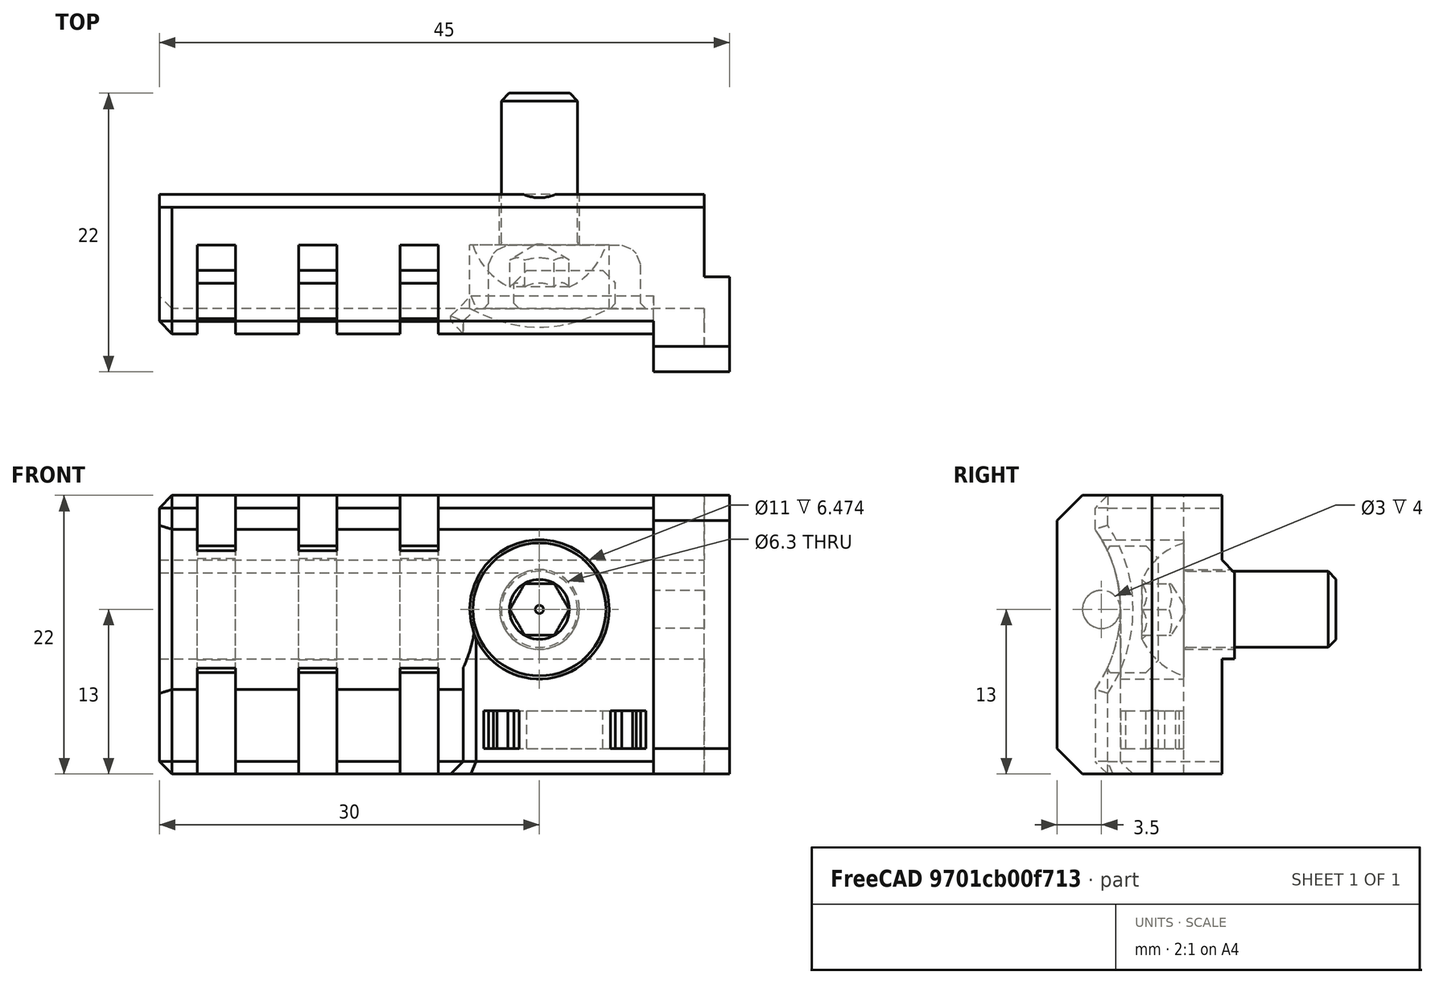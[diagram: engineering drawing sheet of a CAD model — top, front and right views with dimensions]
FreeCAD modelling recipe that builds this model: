
FCSTD DOCUMENT  (FreeCAD 0.19R24291 (Git))
Label: extruder-end-cable-mount
License: Other
LicenseURL: GPL3
objects: Part::Box×11, Part::Chamfer×8, Part::MultiFuse×6, Part::Cut×6, Part::Cylinder×4, Part::Feature×3, Part::FeaturePython×1, Part::Refine×1, App::Part×1
note: 40 computed .brp shape members not serialized (recipe doc carries the construction recipe); baked Part::Feature solids carry a one-line shape summary decoded from their .brp

FEATURE [Part::Box] Box  label="Cube"
  AttacherType = Attacher::AttachEngine3D
  Height = 26
  Length = 10
  Placement = pos=(-2,4.5,0) rot=(0,0,1;0rad)
  Width = 10
FEATURE [Part::Box] Box001  label="Cube001"
  AttacherType = Attacher::AttachEngine3D
  Height = 22
  Length = 45
  Placement = pos=(-45,0,0) rot=(0,0,1;0rad)
  Width = 10
FEATURE [Part::Cylinder] Cylinder
  Angle = 360
  AttacherType = Attacher::AttachEngine3D
  Height = 39
  Placement = pos=(-6,-9,13) rot=(0,-1,0;1.5708rad)
  Radius = 11
FEATURE [Part::Cylinder] Cylinder001
  Angle = 360
  AttacherType = Attacher::AttachEngine3D
  Height = 10
  Placement = pos=(-2,0.5,13) rot=(0,-1,0;1.5708rad)
  Radius = 1.5
FEATURE [Part::Box] Box002  label="Cube002"
  AttacherType = Attacher::AttachEngine3D
  Height = 13
  Length = 15
  Placement = pos=(-18,-7,0) rot=(0,0,1;0rad)
  Width = 10
FEATURE [Part::Chamfer] Chamfer001
  Base = -> Box002
  Edges = 1 edges r=1: [Edge3]
  Placement = pos=(-3,-1,0) rot=(0,0,1;0rad)
FEATURE [Part::Box] Box004  label="Cube004"
  AttacherType = Attacher::AttachEngine3D
  Height = 26
  Length = 3
  Placement = pos=(-32,5,0) rot=(0,0,1;0rad)
  Width = 2
FEATURE [Part::Cylinder] Cylinder002
  Angle = 360
  AttacherType = Attacher::AttachEngine3D
  Height = 10
  Placement = pos=(-13,3e-15,13) rot=(-1,0,0;1.5708rad)
  Radius = 3.15
FEATURE [Part::Cylinder] Cylinder003
  Angle = 360
  AttacherType = Attacher::AttachEngine3D
  Height = 10
  Placement = pos=(-13,-10,13) rot=(-1,0,0;1.5708rad)
  Radius = 5.5
FEATURE [Part::MultiFuse] Fusion
  Placement = pos=(-2,7,0) rot=(0,0,1;0rad)
  Shapes = -> [Cylinder002,Cylinder003]
FEATURE [Part::Box] Box005  label="Cube005"
  AttacherType = Attacher::AttachEngine3D
  Height = 8
  Length = 3
  Placement = pos=(-32,-4,0) rot=(0,0,1;0rad)
  Width = 11
FEATURE [Part::Box] Box006  label="Cube006"
  AttacherType = Attacher::AttachEngine3D
  Height = 8
  Length = 3
  Placement = pos=(-32,-4,18) rot=(0,0,1;0rad)
  Width = 11
FEATURE [Part::Box] Box007  label="Cube007"
  AttacherType = Attacher::AttachEngine3D
  Height = 7.8
  Length = 43
  Placement = pos=(-45,9,9.1) rot=(0,0,1;0rad)
  Width = 2
FEATURE [Part::Box] Box008  label="Cube008"
  AttacherType = Attacher::AttachEngine3D
  Height = 3
  Length = 8
  Width = 2
FEATURE [Part::Box] Box009  label="Cube009"
  AttacherType = Attacher::AttachEngine3D
  Height = 3
  Length = 2
  Placement = pos=(-2,-7,0) rot=(0,0,1;0rad)
  Width = 9
FEATURE [Part::Box] Box010  label="Cube010"
  AttacherType = Attacher::AttachEngine3D
  Height = 3
  Length = 2
  Placement = pos=(8,-7,0) rot=(0,0,1;0rad)
  Width = 9
FEATURE [Part::MultiFuse] Fusion001004
  Shapes = -> [Box009,Box008,Box010]
FEATURE [Part::Chamfer] Chamfer005
  Base = -> Fusion001004
  Edges = 4 edges r=1: [Edge3,Edge15,Edge23,Edge29]
FEATURE [Part::Chamfer] Chamfer006
  Base = -> Chamfer005
  Edges = 4 edges r=0.5: [Edge4,Edge12,Edge47,Edge50]
  Placement = pos=(-17,5,2) rot=(0,0,1;0rad)
FEATURE [Part::FeaturePython] Screw  label="M6x12-Screw"  # Fasteners workbench fastener (typed FeaturePython)
  Placement = pos=(-15,7,13) rot=(1,0,0;1.5708rad)
  diameter = 4
  invert = true
  length = 1
  lengthCustom = 12
  matchOuter = true
  offset = 0
  thread = false
  type = 39
FEATURE [Part::Chamfer] Chamfer007
  Base = -> Box007
  Edges = 1 edges r=1: [Edge12]
FEATURE [Part::Cut] Cut
  Base = -> Box001
  Tool = -> Cylinder
FEATURE [Part::Cut] Cut001
  Base = -> Cut
  Tool = -> Box
FEATURE [Part::Box] Box011  label="Cube011"
  AttacherType = Attacher::AttachEngine3D
  Height = 22
  Length = 6
  Placement = pos=(-6,-3,0) rot=(0,0,1;0rad)
  Width = 3
FEATURE [Part::Chamfer] Chamfer
  Base = -> Box011
  Edges = 2 edges r=2: [Edge9,Edge10]
FEATURE [Part::Cut] Cut002
  Base = -> Cut001
  Tool = -> Chamfer001
FEATURE [Part::MultiFuse] Fusion001007
  Shapes = -> [Cut002,Chamfer]
FEATURE [Part::MultiFuse] Fusion001008
  Placement = pos=(-2,0,0) rot=(0,0,1;0rad)
  Shapes = -> [Box005,Box006,Box004]
FEATURE [Part::Feature] Fusion001008001
  Placement = pos=(-10,0,0) rot=(0,0,1;0rad)
  shape: bbox 3 x 11 x 26 mm, 22 faces (baked)
FEATURE [Part::Feature] Fusion001008002
  Placement = pos=(6,0,0) rot=(0,0,1;0rad)
  shape: bbox 3 x 11 x 26 mm, 22 faces (baked)
FEATURE [Part::Chamfer] Chamfer009001002
  Base = -> Fusion001007
  Edges = 10 edges r=1: [Edge1,Edge2,Edge3,Edge4,Edge6,Edge9,Edge16,Edge29,Edge30,Edge31]
FEATURE [Part::MultiFuse] Fusion001008003
  Shapes = -> [Fusion001008001,Fusion001008,Fusion001008002,Chamfer006]
FEATURE [Part::Cut] Cut003
  Base = -> Chamfer009001002
  Tool = -> Fusion001008003
FEATURE [Part::MultiFuse] Fusion001008004
  Shapes = -> [Cut003,Chamfer007]
FEATURE [Part::Cut] Cut004
  Base = -> Fusion001008004
  Tool = -> Fusion
FEATURE [Part::Cut] Cut005
  Base = -> Cut004
  Tool = -> Cylinder001
FEATURE [Part::Chamfer] Chamfer009001003
  Base = -> Cut005
  Edges = 6 edges r=1: [Edge217,Edge227,Edge237,Edge240,Edge241,Edge242]
FEATURE [Part::Chamfer] Chamfer009001004
  Base = -> Chamfer009001003
  Edges = 10 edges r=0.4: [Edge9,Edge24,Edge28,Edge32,Edge38,Edge42,Edge111,Edge113,Edge115,Edge117]
FEATURE [Part::Refine] Chamfer009001004001
  Source = -> Chamfer009001004
FEATURE [Part::Feature] Chamfer009001004001001
  shape: bbox 45 x 14 x 22 mm, 100 faces (baked)
FEATURE [App::Part] Part  label="extruder-cable-end-mounter"
  Group = -> [Screw,Chamfer009001004001001]
  Origin = -> Origin
